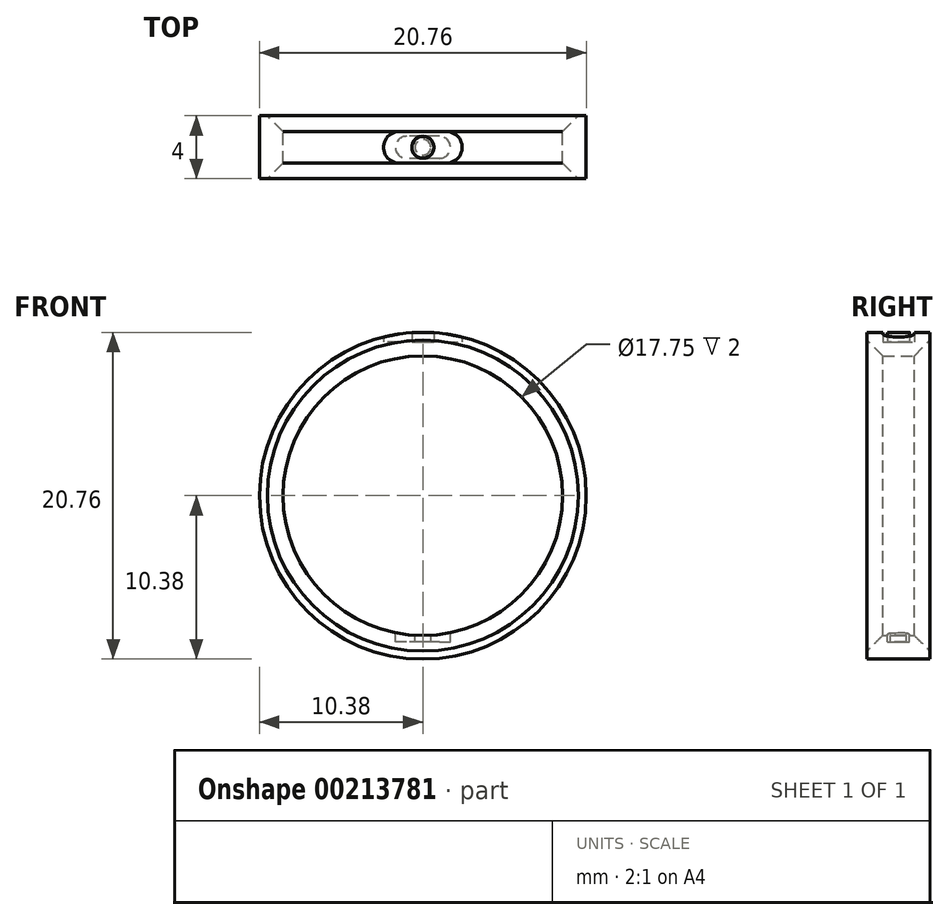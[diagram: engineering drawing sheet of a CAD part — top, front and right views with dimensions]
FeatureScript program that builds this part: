
annotation { "Feature Type Name" : "Feature", "Feature Type Description" : "" }
export const myFeature = defineFeature(function(context is Context, id is Id, definition is map)
    precondition{}
    {
        {
            var Q0;
            Q0=qCreatedBy(makeId("Front.planeOp"),FACE);
            var sketch = newSketch(context, id + "F0", { "sketchPlane" : qUnion([Q0])});
            skCircle(sketch, "E0", {"center": v(0, 0) * mm, "radius": 8.88 * mm});
            skCircle(sketch, "E1.0", {"center": v(0, 0) * mm, "radius": 10.38 * mm});
            skSolve(sketch);
        }
        {
            var Q0;
            Q0=makeQuery(id+"F0.imprint","IMPRINT",FACE,{"disambiguationData":[TD([[makeQuery(id+"F0.imprint","IMPRINT",EDGE,{"derivedFrom":sQuery(id+"F0.wireOp",EDGE,"E0")}),-1.0]])]});
            extrude(context, id + "F1", {"entities" : qUnion([Q0]), "depth" : 2 * mm, "hasSecondDirection" : true, "secondDirectionOppositeDirection" : true, "secondDirectionDepth" : 2 * mm, "offsetDistance" : 25 * mm});
        }
        {
            var Q0;
            Q0=makeQuery(id+"F1.opExtrude","CAP_EDGE",EDGE,{"disambiguationData":[OSD([sQuery(id+"F0.wireOp",EDGE,"E0")])],"isStart":false});
            var Q1;
            Q1=makeQuery(id+"F1.opExtrude","CAP_EDGE",EDGE,{"disambiguationData":[OSD([sQuery(id+"F0.wireOp",EDGE,"E0")])],"isStart":true});
            chamfer(context, id + "F2", {"entities" : qUnion([Q0, Q1]), "width" : 1 * mm, "tangentPropagation" : true});
        }
        {
            var Q0;
            Q0=qCreatedBy(makeId("Top.planeOp"),FACE);
            var sketch = newSketch(context, id + "F3", { "sketchPlane" : qUnion([Q0])});
            skLineSegment(sketch, "E2.bottom", {"start": v(1.5, -1) * mm, "end": v(-1.5, -1) * mm});
            skLineSegment(sketch, "E2.top", {"start": v(1.5, 1) * mm, "end": v(-1.5, 1) * mm});
            skLineSegment(sketch, "E2.left", {"start": v(2.5, 0) * mm, "end": v(2.5, 0) * mm});
            skLineSegment(sketch, "E2.right", {"start": v(-2.5, 0) * mm, "end": v(-2.5, 0) * mm});
            skPoint(sketch, "E2.middle", {"position": v(0, 0) * mm});
            skPoint(sketch, "E3.visualSharp", {"position": v(2.5, 1) * mm});
            skArc(sketch, "E3.filletArc", {"start": v(2.5, 0) * mm, "mid": v(2.2, 0.7) * mm, "end": v(1.5, 1) * mm});
            skPoint(sketch, "E4.visualSharp", {"position": v(2.5, -1) * mm});
            skArc(sketch, "E4.filletArc", {"start": v(1.5, -1) * mm, "mid": v(2.2, -0.7) * mm, "end": v(2.5, 0) * mm});
            skPoint(sketch, "E5.visualSharp", {"position": v(-2.5, -1) * mm});
            skArc(sketch, "E5.filletArc", {"start": v(-2.5, 0) * mm, "mid": v(-2.2, -0.7) * mm, "end": v(-1.5, -1) * mm});
            skPoint(sketch, "E6.visualSharp", {"position": v(-2.5, 1) * mm});
            skArc(sketch, "E6.filletArc", {"start": v(-1.5, 1) * mm, "mid": v(-2.2, 0.7) * mm, "end": v(-2.5, 0) * mm});
            skCircle(sketch, "E7", {"center": v(0, 0) * mm, "radius": 0.7 * mm});
            skSolve(sketch);
        }
        {
            var Q0;
            Q0=makeQuery(id+"F3.imprint","IMPRINT",FACE,{"disambiguationData":[TD([[makeQuery(id+"F3.imprint","IMPRINT",EDGE,{"derivedFrom":sQuery(id+"F3.wireOp",EDGE,"E2.bottom")}),-1.0]])]});
            extrude(context, id + "F4", {"entities" : qUnion([Q0]), "operationType" : NewBodyOperationType.REMOVE, "depth" : 25 * mm, "hasSecondDirection" : true, "secondDirectionOppositeDirection" : false, "secondDirectionDepth" : (17.75 / 2 + .9) * mm});
        }
        {
            var Q0;
            Q0=qCreatedBy(makeId("Top.planeOp"),FACE);
            var sketch = newSketch(context, id + "F5", { "sketchPlane" : qUnion([Q0])});
            skLineSegment(sketch, "E8.bottom", {"start": v(1.06, 0.7) * mm, "end": v(-1.04, 0.7) * mm});
            skArc(sketch, "E9.filletArc", {"start": v(1.06, -0.7) * mm, "mid": v(1.55, -0.5) * mm, "end": v(1.76, 0) * mm});
            skArc(sketch, "E10.filletArc", {"start": v(1.76, 0) * mm, "mid": v(1.55, 0.5) * mm, "end": v(1.06, 0.7) * mm});
            skArc(sketch, "E11.filletArc", {"start": v(-1.74, 0) * mm, "mid": v(-1.53, -0.5) * mm, "end": v(-1.04, -0.7) * mm});
            skArc(sketch, "E12.filletArc", {"start": v(-1.04, 0.7) * mm, "mid": v(-1.53, 0.5) * mm, "end": v(-1.74, 0) * mm});
            skLineSegment(sketch, "E13.bottom", {"start": v(1.03, 2.97) * mm, "end": v(-1.07, 2.97) * mm});
            skLineSegment(sketch, "E13.top", {"start": v(1.03, 1.57) * mm, "end": v(-1.07, 1.57) * mm});
            skArc(sketch, "E14.filletArc", {"start": v(1.03, 1.57) * mm, "mid": v(1.52, 1.77) * mm, "end": v(1.73, 2.27) * mm});
            skArc(sketch, "E15.filletArc", {"start": v(1.73, 2.27) * mm, "mid": v(1.52, 2.76) * mm, "end": v(1.03, 2.97) * mm});
            skArc(sketch, "E16.filletArc", {"start": v(-1.77, 2.27) * mm, "mid": v(-1.56, 1.77) * mm, "end": v(-1.07, 1.57) * mm});
            skArc(sketch, "E17.filletArc", {"start": v(-1.07, 2.97) * mm, "mid": v(-1.56, 2.76) * mm, "end": v(-1.77, 2.27) * mm});
            skLineSegment(sketch, "E18", {"start": v(1.06, -0.7) * mm, "end": v(-1.04, -0.7) * mm});
            skCircle(sketch, "E19", {"center": v(0, 0) * mm, "radius": 0.5 * mm});
            skLineSegment(sketch, "E20.bottom", {"start": v(1.03, -1.54) * mm, "end": v(-1.07, -1.54) * mm});
            skLineSegment(sketch, "E20.top", {"start": v(1.03, -2.94) * mm, "end": v(-1.07, -2.94) * mm});
            skArc(sketch, "E21.filletArc", {"start": v(1.03, -2.94) * mm, "mid": v(1.52, -2.73) * mm, "end": v(1.73, -2.24) * mm});
            skArc(sketch, "E22.filletArc", {"start": v(1.73, -2.24) * mm, "mid": v(1.52, -1.74) * mm, "end": v(1.03, -1.54) * mm});
            skArc(sketch, "E23.filletArc", {"start": v(-1.77, -2.24) * mm, "mid": v(-1.56, -2.73) * mm, "end": v(-1.07, -2.94) * mm});
            skArc(sketch, "E24.filletArc", {"start": v(-1.07, -1.54) * mm, "mid": v(-1.56, -1.74) * mm, "end": v(-1.77, -2.24) * mm});
            skSolve(sketch);
        }
        {
            var Q0;
            Q0=makeQuery(id+"F5.imprint","IMPRINT",FACE,{"disambiguationData":[TD([[makeQuery(id+"F5.imprint","IMPRINT",EDGE,{"derivedFrom":sQuery(id+"F5.wireOp",EDGE,"E20.bottom")}),1.0]])]});
            var Q1;
            Q1=makeQuery(id+"F5.imprint","IMPRINT",FACE,{"disambiguationData":[TD([[makeQuery(id+"F5.imprint","IMPRINT",EDGE,{"derivedFrom":sQuery(id+"F5.wireOp",EDGE,"E8.bottom")}),1.0]])]});
            var Q2;
            Q2=makeQuery(id+"F5.imprint","IMPRINT",FACE,{"disambiguationData":[TD([[makeQuery(id+"F5.imprint","IMPRINT",EDGE,{"derivedFrom":sQuery(id+"F5.wireOp",EDGE,"E13.bottom")}),1.0]])]});
            extrude(context, id + "F6", {"entities" : qUnion([Q0, Q1, Q2]), "operationType" : NewBodyOperationType.REMOVE, "oppositeDirection" : true, "depth" : 9.3 * mm, "offsetDistance" : 25 * mm});
        }
    });
